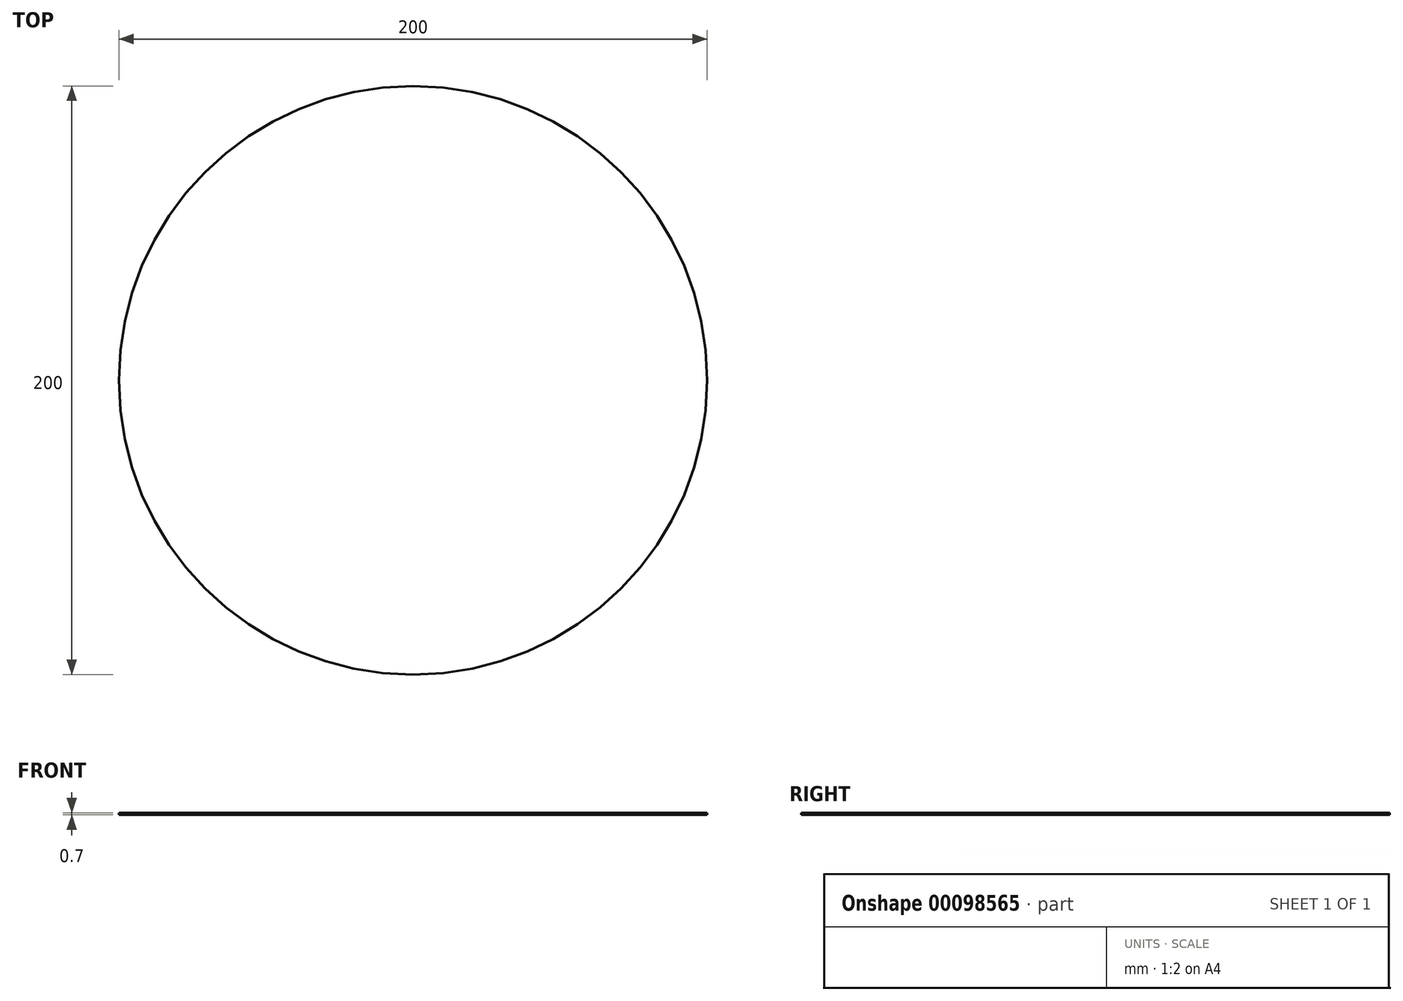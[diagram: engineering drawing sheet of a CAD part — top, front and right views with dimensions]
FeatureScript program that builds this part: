
annotation { "Feature Type Name" : "Feature", "Feature Type Description" : "" }
export const myFeature = defineFeature(function(context is Context, id is Id, definition is map)
    precondition{}
    {
        {
            var Q0;
            Q0=qCreatedBy(makeId("Top.planeOp"),FACE);
            var sketch = newSketch(context, id + "F0", { "sketchPlane" : qUnion([Q0])});
            skCircle(sketch, "E0", {"center": v(0, 0) * mm, "radius": 100 * mm});
            skSolve(sketch);
        }
        {
            var Q0;
            Q0=makeQuery(id+"F0.imprint","IMPRINT",FACE,{"disambiguationData":[TD([[makeQuery(id+"F0.imprint","IMPRINT",EDGE,{"derivedFrom":sQuery(id+"F0.wireOp",EDGE,"E0")}),1.0]])]});
            extrude(context, id + "F1", {"entities" : qUnion([Q0]), "depth" : 0.7 * mm});
        }
    });
